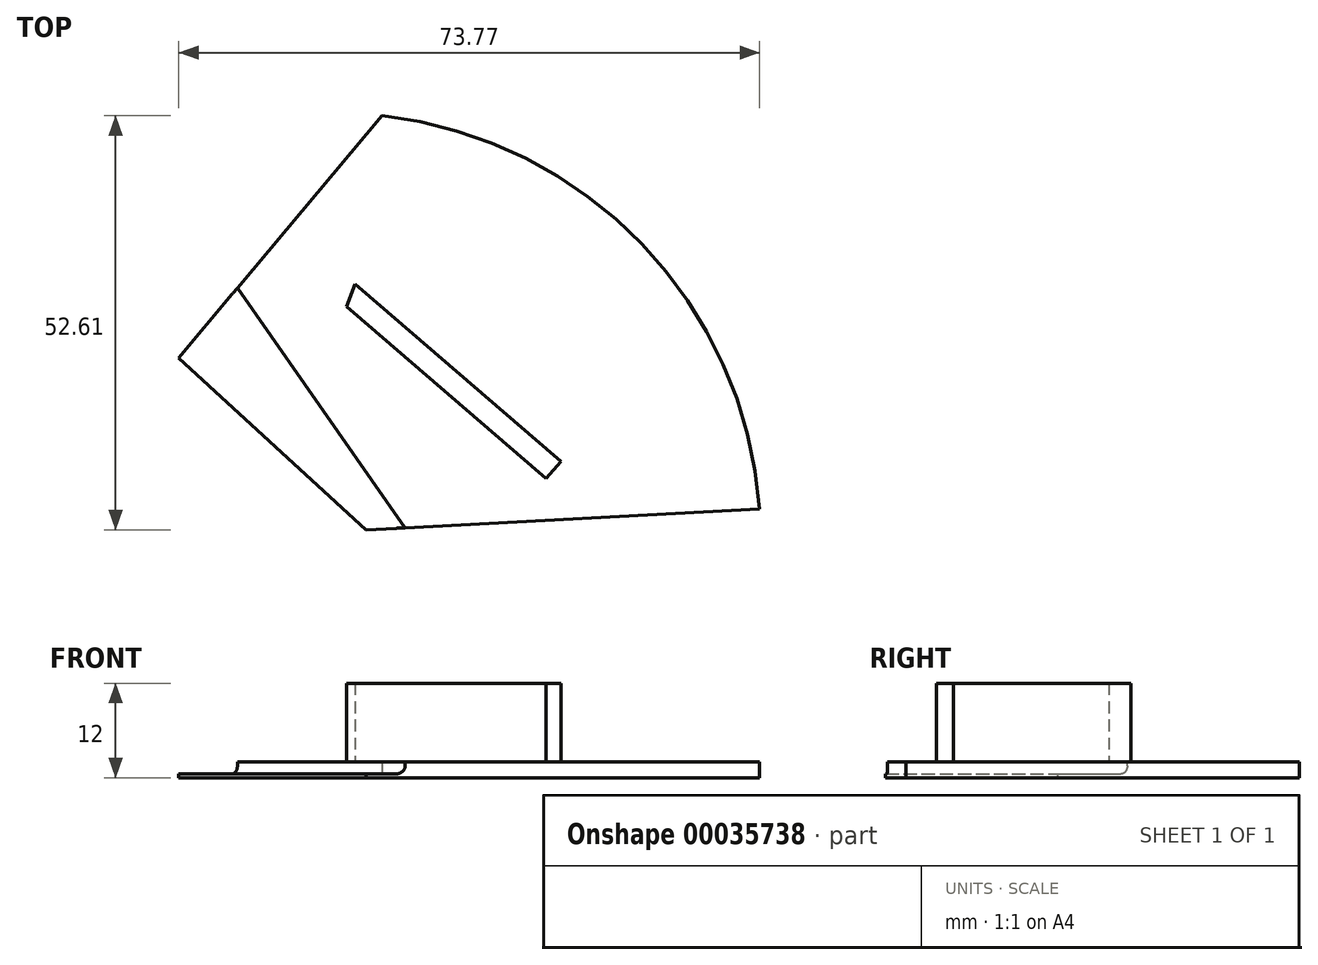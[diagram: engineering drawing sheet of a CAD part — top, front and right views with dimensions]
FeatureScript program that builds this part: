
annotation { "Feature Type Name" : "Feature", "Feature Type Description" : "" }
export const myFeature = defineFeature(function(context is Context, id is Id, definition is map)
    precondition{}
    {
        {
            var Q0;
            Q0=qCreatedBy(makeId("Top.planeOp"),FACE);
            var sketch = newSketch(context, id + "F0", { "sketchPlane" : qUnion([Q0])});
            skArc(sketch, "E0", {"start": v(47.9, 2.63) * mm, "mid": v(32.98, 36.28) * mm, "end": v(0, 52.61) * mm});
            skLineSegment(sketch, "E1", {"start": v(47.9, 2.63) * mm, "end": v(-2.08, 0) * mm});
            skLineSegment(sketch, "E2", {"start": v(-2.08, 0) * mm, "end": v(-25.87, 21.85) * mm});
            skLineSegment(sketch, "E3", {"start": v(-25.87, 21.85) * mm, "end": v(0, 52.61) * mm});
            skSolve(sketch);
        }
        {
            var Q0;
            Q0=makeQuery(id+"F0.imprint","IMPRINT",FACE,{"disambiguationData":[TD([[makeQuery(id+"F0.imprint","IMPRINT",EDGE,{"derivedFrom":sQuery(id+"F0.wireOp",EDGE,"E0")}),1.0]])]});
            extrude(context, id + "F1", {"entities" : qUnion([Q0]), "depth" : 2 * mm});
        }
        {
            var Q0;
            Q0=makeQuery(id+"F1.opExtrude","CAP_FACE",FACE,{"disambiguationData":[OSD([sQuery(id+"F0.wireOp",EDGE,"E0"),sQuery(id+"F0.wireOp",EDGE,"E1"),sQuery(id+"F0.wireOp",EDGE,"E2"),sQuery(id+"F0.wireOp",EDGE,"E3")])],"isStart":false});
            var sketch = newSketch(context, id + "F2", { "sketchPlane" : qUnion([Q0])});
            skLineSegment(sketch, "E4", {"start": v(-4.56, 28.4) * mm, "end": v(20.82, 6.5) * mm});
            skLineSegment(sketch, "E5", {"start": v(20.82, 6.5) * mm, "end": v(22.67, 8.66) * mm});
            skLineSegment(sketch, "E6", {"start": v(22.67, 8.66) * mm, "end": v(-3.48, 31.21) * mm});
            skLineSegment(sketch, "E7", {"start": v(-3.48, 31.21) * mm, "end": v(-4.56, 28.4) * mm});
            skSolve(sketch);
        }
        {
            var Q0;
            Q0 = qSketchRegion(id + "F2", true);
            extrude(context, id + "F3", {"entities" : qUnion([Q0]), "operationType" : NewBodyOperationType.ADD, "depth" : 10 * mm});
        }
        {
            var Q0;
            Q0=makeQuery(id+"F1.opExtrude","CAP_FACE",FACE,{"disambiguationData":[OSD([sQuery(id+"F0.wireOp",EDGE,"E0"),sQuery(id+"F0.wireOp",EDGE,"E1"),sQuery(id+"F0.wireOp",EDGE,"E2"),sQuery(id+"F0.wireOp",EDGE,"E3")])],"isStart":false});
            var sketch = newSketch(context, id + "F4", { "sketchPlane" : qUnion([Q0])});
            skLineSegment(sketch, "E8", {"start": v(2.9, 0.26) * mm, "end": v(-18.4, 30.73) * mm});
            skSolve(sketch);
        }
        {
            var Q0;
            {var subQ1=sQuery(id+"F4.wireOp",EDGE,"E8");Q0=makeQuery(id+"F4.imprint","IMPRINT",FACE,{"disambiguationData":[TD([[makeQuery(id+"F4.imprint","IMPRINT",EDGE,{"derivedFrom":subQ1}),1.0]])]});}
            extrude(context, id + "F5", {"entities" : qUnion([Q0]), "operationType" : NewBodyOperationType.REMOVE, "oppositeDirection" : true, "depth" : 1 * mm});
        }
        {
            var Q0;
            Q0=makeQuery(id+"F5.boolean.opBoolean","COPY",FACE,{"derivedFrom":makeQuery(id+"F5.opExtrude","CAP_FACE",FACE,{"disambiguationData":[OSD([sQuery(id+"F0.wireOp",EDGE,"E1"),sQuery(id+"F0.wireOp",EDGE,"E2"),sQuery(id+"F0.wireOp",EDGE,"E3"),sQuery(id+"F4.wireOp",EDGE,"E8")])],"isStart":false})});
            extrude(context, id + "F6", {"entities" : qUnion([Q0]), "operationType" : NewBodyOperationType.REMOVE, "oppositeDirection" : true, "depth" : 0.5 * mm});
        }
        {
            var Q0;
            Q0=makeQuery(id+"F6.boolean.opBoolean","COPY",EDGE,{"derivedFrom":makeQuery(id+"F6.opExtrude","CAP_EDGE",EDGE,{"disambiguationData":[OSD([sQuery(id+"F4.wireOp",EDGE,"E8")])],"isStart":false})});
            fillet(context, id + "F7", {"entities" : qUnion([Q0]), "radius" : 1 * mm, "tangentPropagation" : true, "allowEdgeOverflow" : false});
        }
    });
